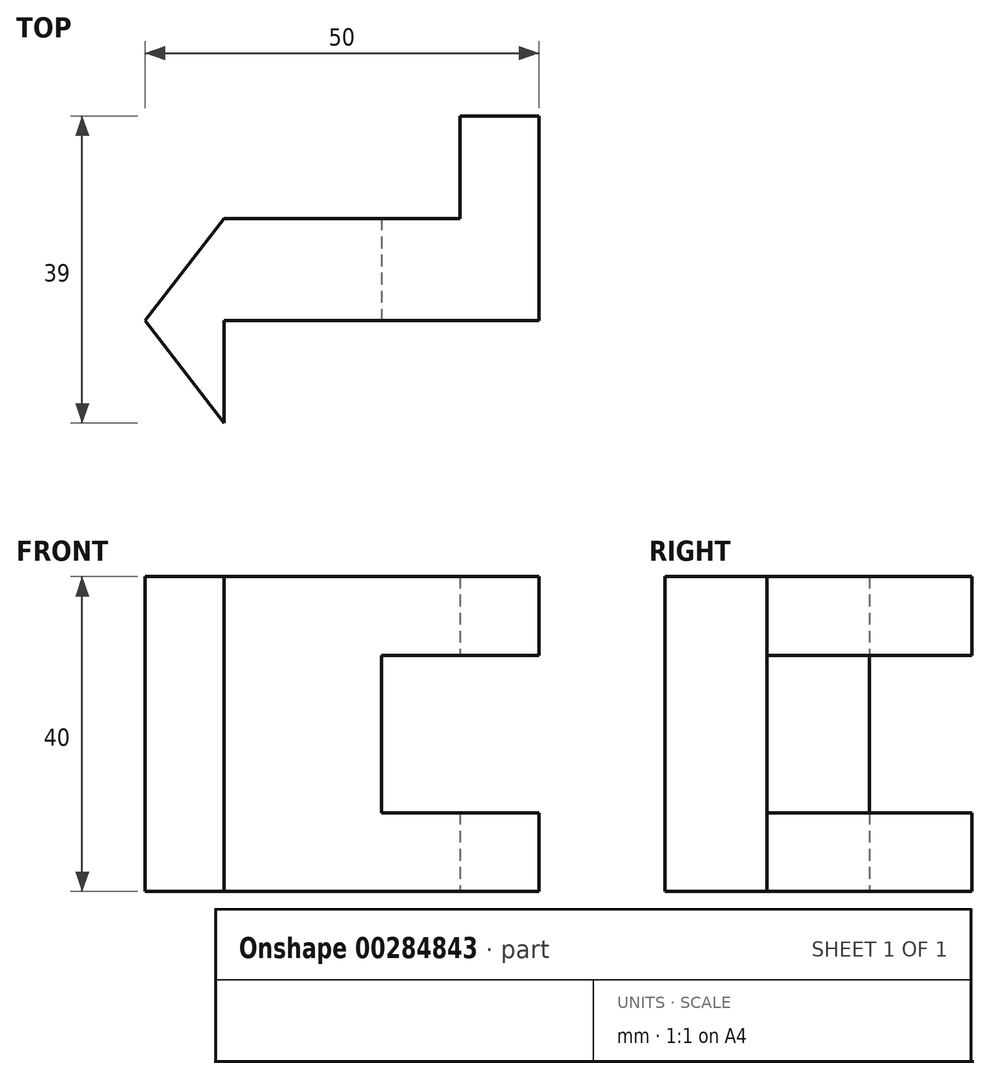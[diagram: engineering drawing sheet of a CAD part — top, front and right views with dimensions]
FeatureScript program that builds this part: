
annotation { "Feature Type Name" : "Feature", "Feature Type Description" : "" }
export const myFeature = defineFeature(function(context is Context, id is Id, definition is map)
    precondition{}
    {
        {
            var Q0;
            Q0=qCreatedBy(makeId("Top.planeOp"),FACE);
            var sketch = newSketch(context, id + "F0", { "sketchPlane" : qUnion([Q0])});
            skLineSegment(sketch, "E0.bottom", {"start": v(0, 0) * mm, "end": v(50, 0) * mm});
            skLineSegment(sketch, "E0.top", {"start": v(0, 39) * mm, "end": v(50, 39) * mm});
            skLineSegment(sketch, "E0.left", {"start": v(0, 0) * mm, "end": v(0, 39) * mm});
            skLineSegment(sketch, "E0.right", {"start": v(50, 0) * mm, "end": v(50, 39) * mm});
            skLineSegment(sketch, "E1", {"start": v(10, 0) * mm, "end": v(10, 13) * mm});
            skLineSegment(sketch, "E2", {"start": v(10, 13) * mm, "end": v(50, 13) * mm});
            skLineSegment(sketch, "E3", {"start": v(40, 39) * mm, "end": v(40, 26) * mm});
            skLineSegment(sketch, "E4", {"start": v(40, 26) * mm, "end": v(0, 26) * mm});
            skSolve(sketch);
        }
        {
            var Q0;
            {var subQ9=sQuery(id+"F0.wireOp",EDGE,"E1");Q0=makeQuery(id+"F0.imprint","IMPRINT",FACE,{"disambiguationData":[TD([[makeQuery(id+"F0.imprint","IMPRINT",EDGE,{"derivedFrom":subQ9}),1.0]])]});}
            extrude(context, id + "F1", {"entities" : qUnion([Q0]), "depth" : 40 * mm, "symmetric" : true});
        }
        {
            var Q0;
            Q0=makeQuery(id+"F1.opExtrude","SWEPT_FACE",FACE,{"disambiguationData":[OSD([sQuery(id+"F0.wireOp",EDGE,"E2")])]});
            var sketch = newSketch(context, id + "F2", { "sketchPlane" : qUnion([Q0])});
            skLineSegment(sketch, "E5.bottom", {"start": v(50, 10) * mm, "end": v(30, 10) * mm});
            skLineSegment(sketch, "E5.top", {"start": v(50, -10) * mm, "end": v(30, -10) * mm});
            skLineSegment(sketch, "E5.left", {"start": v(50, 10) * mm, "end": v(50, -10) * mm});
            skLineSegment(sketch, "E5.right", {"start": v(30, 10) * mm, "end": v(30, -10) * mm});
            skSolve(sketch);
        }
        {
            var Q0;
            Q0=qSketchRegion(id+"F2",true);
            extrude(context, id + "F3", {"entities" : qUnion([Q0]), "operationType" : NewBodyOperationType.REMOVE, "endBound" : BoundingType.THROUGH_ALL, "oppositeDirection" : true, "depth" : 25 * mm});
        }
        {
            var Q0;
            Q0=makeQuery(id+"F1.opExtrude","CAP_FACE",FACE,{"disambiguationData":[OSD([sQuery(id+"F0.wireOp",EDGE,"E0.bottom"),sQuery(id+"F0.wireOp",EDGE,"E0.top"),sQuery(id+"F0.wireOp",EDGE,"E0.left"),sQuery(id+"F0.wireOp",EDGE,"E0.right"),sQuery(id+"F0.wireOp",EDGE,"E1"),sQuery(id+"F0.wireOp",EDGE,"E2"),sQuery(id+"F0.wireOp",EDGE,"E3"),sQuery(id+"F0.wireOp",EDGE,"E4")])],"isStart":false});
            var sketch = newSketch(context, id + "F4", { "sketchPlane" : qUnion([Q0])});
            skLineSegment(sketch, "E6", {"start": v(10, 0) * mm, "end": v(0, 13) * mm});
            skLineSegment(sketch, "E7", {"start": v(0, 13) * mm, "end": v(0, 0) * mm});
            skLineSegment(sketch, "E8", {"start": v(0, 0) * mm, "end": v(10, 0) * mm});
            skSolve(sketch);
        }
        {
            var Q0;
            Q0=qSketchRegion(id+"F4",true);
            extrude(context, id + "F5", {"entities" : qUnion([Q0]), "operationType" : NewBodyOperationType.REMOVE, "endBound" : BoundingType.THROUGH_ALL, "oppositeDirection" : true, "depth" : 25 * mm});
        }
        {
            var Q0;
            Q0=makeQuery(id+"F1.opExtrude","CAP_FACE",FACE,{"disambiguationData":[OSD([sQuery(id+"F0.wireOp",EDGE,"E0.bottom"),sQuery(id+"F0.wireOp",EDGE,"E0.top"),sQuery(id+"F0.wireOp",EDGE,"E0.left"),sQuery(id+"F0.wireOp",EDGE,"E0.right"),sQuery(id+"F0.wireOp",EDGE,"E1"),sQuery(id+"F0.wireOp",EDGE,"E2"),sQuery(id+"F0.wireOp",EDGE,"E3"),sQuery(id+"F0.wireOp",EDGE,"E4")])],"isStart":false});
            var sketch = newSketch(context, id + "F6", { "sketchPlane" : qUnion([Q0])});
            skLineSegment(sketch, "E9", {"start": v(10, 26) * mm, "end": v(0, 13) * mm});
            skLineSegment(sketch, "E10", {"start": v(0, 13) * mm, "end": v(0, 26) * mm});
            skLineSegment(sketch, "E11", {"start": v(0, 26) * mm, "end": v(10, 26) * mm});
            skSolve(sketch);
        }
        {
            var Q0;
            Q0 = qSketchRegion(id + "F6", true);
            extrude(context, id + "F7", {"entities" : qUnion([Q0]), "operationType" : NewBodyOperationType.REMOVE, "endBound" : BoundingType.THROUGH_ALL, "oppositeDirection" : true, "depth" : 25 * mm});
        }
    });
